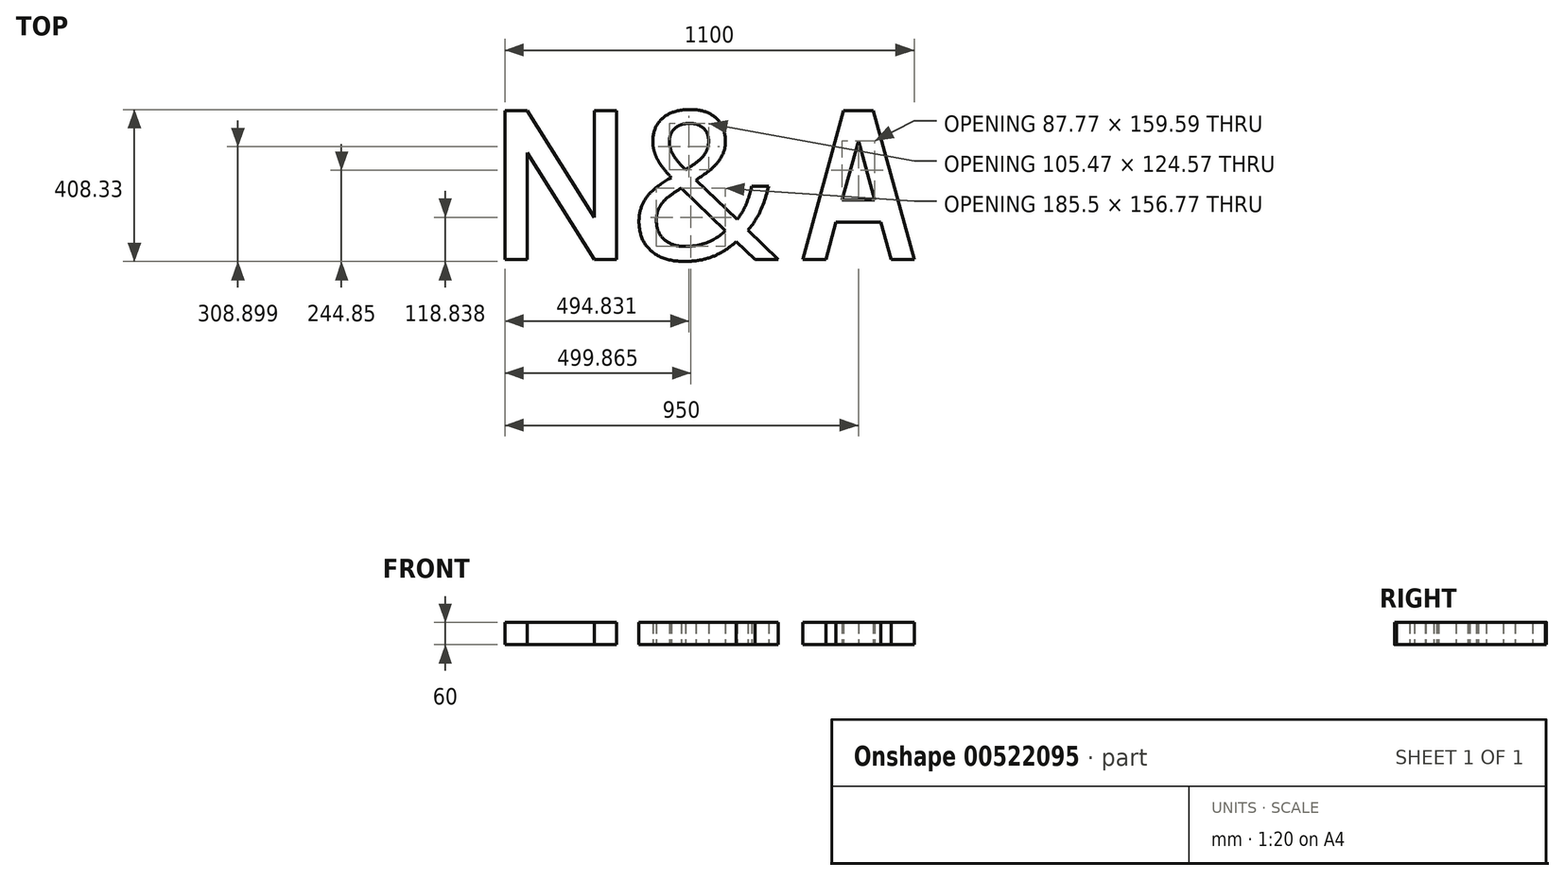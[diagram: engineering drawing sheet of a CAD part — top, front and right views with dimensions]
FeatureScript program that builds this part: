
annotation { "Feature Type Name" : "Feature", "Feature Type Description" : "" }
export const myFeature = defineFeature(function(context is Context, id is Id, definition is map)
    precondition{}
    {
        {
            var Q0;
            Q0=qCreatedBy(makeId("Top.planeOp"),FACE);
            var sketch = newSketch(context, id + "F0", { "sketchPlane" : qUnion([Q0])});
            skLineSegment(sketch, "E0.bottom", {"start": v(0, 0) * mm, "end": v(60, 0) * mm});
            skLineSegment(sketch, "E0.top", {"start": v(0, 400) * mm, "end": v(60, 400) * mm});
            skLineSegment(sketch, "E0.left", {"start": v(0, 0) * mm, "end": v(0, 400) * mm});
            skLineSegment(sketch, "E0.right", {"start": v(60, 0) * mm, "end": v(60, 400) * mm});
            skLineSegment(sketch, "E1.bottom", {"start": v(240, 0) * mm, "end": v(300, 0) * mm});
            skLineSegment(sketch, "E1.top", {"start": v(240, 400) * mm, "end": v(300, 400) * mm});
            skLineSegment(sketch, "E1.left", {"start": v(240, 0) * mm, "end": v(240, 400) * mm});
            skLineSegment(sketch, "E1.right", {"start": v(300, 0) * mm, "end": v(300, 400) * mm});
            skLineSegment(sketch, "E2", {"start": v(60, 400) * mm, "end": v(240, 112.94) * mm});
            skLineSegment(sketch, "E3", {"start": v(240, 112.94) * mm, "end": v(240, 0) * mm});
            skLineSegment(sketch, "E4", {"start": v(240, 0) * mm, "end": v(60, 287.06) * mm});
            skLineSegment(sketch, "E5", {"start": v(910, 400) * mm, "end": v(800, 0) * mm});
            skLineSegment(sketch, "E6", {"start": v(862.23, 0) * mm, "end": v(950, 319.17) * mm});
            skLineSegment(sketch, "E7", {"start": v(950, 319.17) * mm, "end": v(1037.77, 0) * mm});
            skLineSegment(sketch, "E8", {"start": v(990, 400) * mm, "end": v(1100, 0) * mm});
            skLineSegment(sketch, "E9", {"start": v(910, 400) * mm, "end": v(990, 400) * mm});
            skLineSegment(sketch, "E10", {"start": v(800, 0) * mm, "end": v(862.23, 0) * mm});
            skLineSegment(sketch, "E11", {"start": v(1037.77, 0) * mm, "end": v(1100, 0) * mm});
            skLineSegment(sketch, "E12", {"start": v(906.11, 159.59) * mm, "end": v(993.89, 159.59) * mm});
            skLineSegment(sketch, "E13", {"start": v(889.61, 99.59) * mm, "end": v(1010.39, 99.59) * mm});
            skText(sketch, "E14", { "text": "&", "fontName": "OpenSans-Regular.ttf"});
            const initialGuessF0  = {"E14": [0.32977, 0, 1, 0, 0.4]};
            skSetInitialGuess(sketch, initialGuessF0);
            skSolve(sketch);
        }
        {
            var Q0;
            Q0=makeQuery(id+"F0.imprint","IMPRINT",FACE,{"disambiguationData":[TD([[makeQuery(id+"F0.imprint","IMPRINT",EDGE,{"derivedFrom":sQuery(id+"F0.wireOp",EDGE,"E1.bottom")}),1.0]])]});
            var Q1;
            {var subQ0=sQuery(id+"F0.wireOp",EDGE,"E2");Q1=makeQuery(id+"F0.imprint","IMPRINT",FACE,{"disambiguationData":[TD([[makeQuery(id+"F0.imprint","IMPRINT",EDGE,{"derivedFrom":subQ0}),-1.0]])]});}
            var Q2;
            {var subQ1=sQuery(id+"F0.wireOp",EDGE,"E0.bottom");Q2=makeQuery(id+"F0.imprint","IMPRINT",FACE,{"disambiguationData":[TD([[makeQuery(id+"F0.imprint","IMPRINT",EDGE,{"derivedFrom":subQ1}),1.0]])]});}
            extrude(context, id + "F1", {"entities" : qUnion([Q0, Q1, Q2]), "depth" : 60 * mm, "offsetDistance" : 25.4 * mm});
        }
        {
            var Q0;
            Q0 = qSketchRegion(id + "F0", true);
            extrude(context, id + "F2", {"entities" : qUnion([Q0]), "operationType" : NewBodyOperationType.ADD, "depth" : 60 * mm, "offsetDistance" : 25 * mm});
        }
    });
